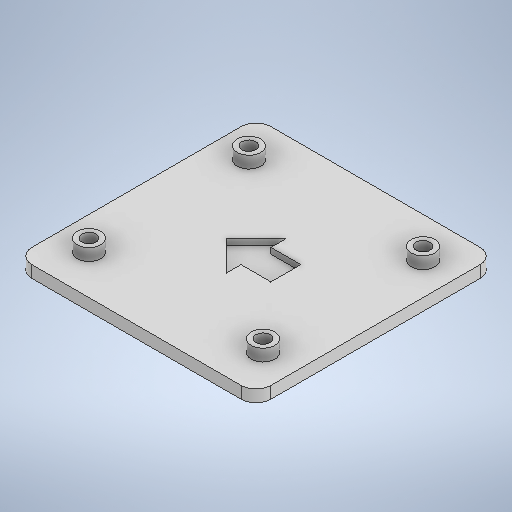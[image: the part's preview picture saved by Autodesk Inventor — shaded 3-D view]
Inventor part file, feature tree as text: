
AUTODESK INVENTOR PART (.ipt)
format: ipt  version: 2025.1 (Build 291241020, 241B)  size: 298,496 bytes
history: native  units: in
note: dims shown in document units (in); Inventor stores cm internally (conversion verified against a paired STEP export)
features: extrude x3, sketch x2, fillet x1
ambient origin geometry x8: Origin, YZ Plane, XZ Plane, XY Plane, X Axis, Y Axis, Z Axis, Center Point
bodies: Solid1 (feature_tree)
feature tree (6):
  sketch  "Sketch1"  dims[d9=2.0in d10=2.0in]
  extrude  "Extrusion1"  Depth=2.0in
  extrude  "Extrusion2"  Depth=0.05in
  fillet  "Fillet1"  Radius=1.3386in
  extrude  "Extrusion4"  Depth=0.05in
  sketch  "Sketch3"  dims[d11=0.1181in d12=0.1181in d13=1.3386in d14=0.1969in d15=0.1969in d16=0.3305in d17=0.118in d18=0.118in d19=0.197in d20=0.197in d21=1.339in d22=1.4567in d23=1.4567in d24=0.2715in d25=0.1in d26=0.0in d27=0.2in d28=0.0in d29=0.125in d40=0.25in d41=0.25in d42=0.25in d43=0.125in d44=45.0deg d45=0.875in d47=0.25in d48=0.75in d49=0.05in d50=0.0in]
